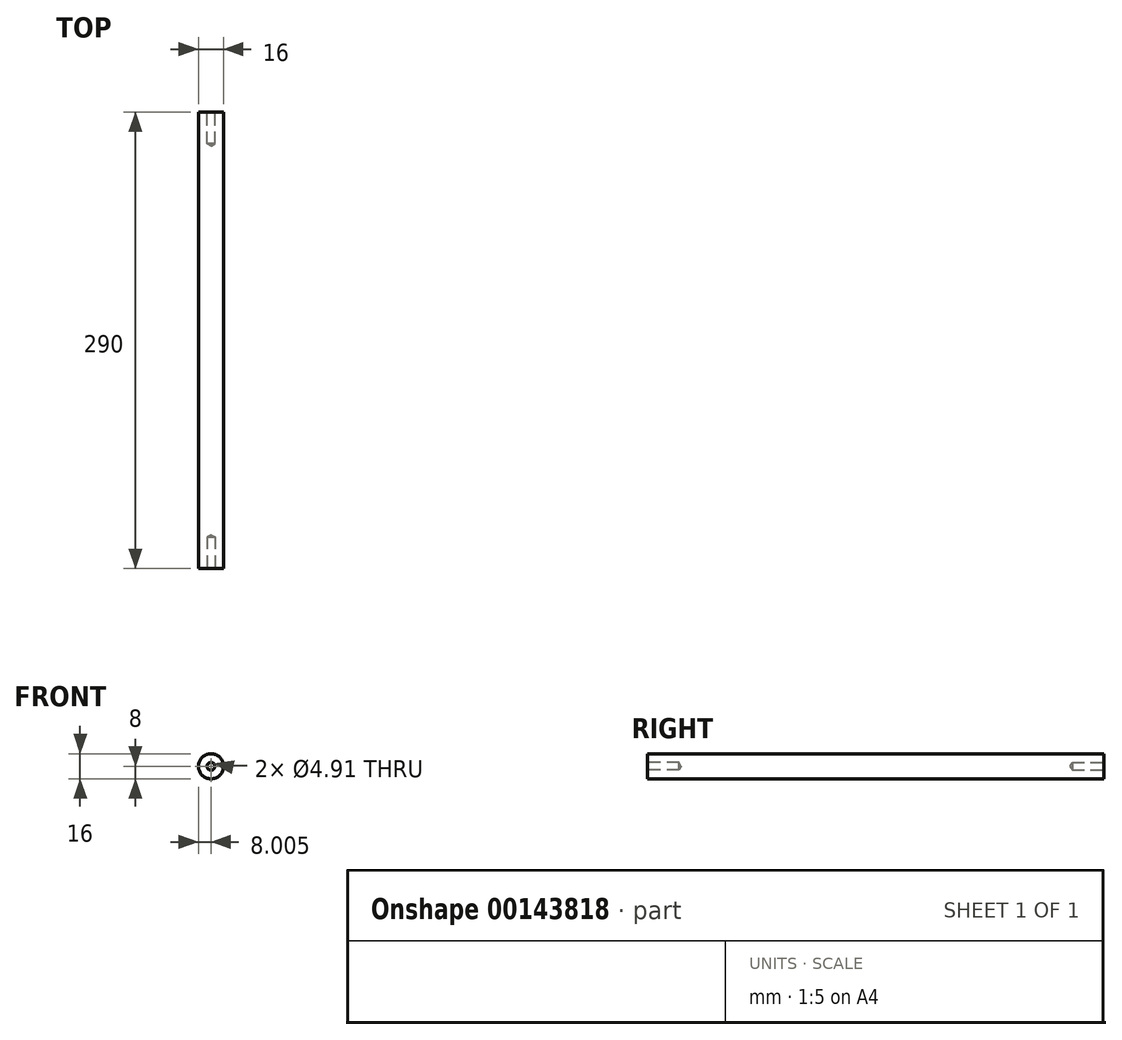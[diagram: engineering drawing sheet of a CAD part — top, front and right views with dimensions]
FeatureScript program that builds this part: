
annotation { "Feature Type Name" : "Feature", "Feature Type Description" : "" }
export const myFeature = defineFeature(function(context is Context, id is Id, definition is map)
    precondition{}
    {
        {
            var Q0;
            Q0=qCreatedBy(makeId("Front.planeOp"),FACE);
            var sketch = newSketch(context, id + "F0", { "sketchPlane" : qUnion([Q0])});
            skCircle(sketch, "E0", {"center": v(-12.95, 5.59) * mm, "radius": 8 * mm});
            skSolve(sketch);
        }
        {
            var Q0;
            Q0=makeQuery(id+"F0.imprint","IMPRINT",FACE,{"disambiguationData":[TD([[makeQuery(id+"F0.imprint","IMPRINT",EDGE,{"derivedFrom":sQuery(id+"F0.wireOp",EDGE,"E0")}),1.0]])]});
            extrude(context, id + "F1", {"entities" : qUnion([Q0]), "depth" : 290 * mm});
        }
        {
            var Q0;
            Q0=makeQuery(id+"F1.opExtrude","CAP_FACE",FACE,{"disambiguationData":[OSD([sQuery(id+"F0.wireOp",EDGE,"E0")])],"isStart":false});
            var sketch = newSketch(context, id + "F2", { "sketchPlane" : qUnion([Q0])});
            skCircle(sketch, "E1", {"center": v(-12.95, 5.59) * mm, "radius": 2.46 * mm});
            skSolve(sketch);
        }
        {
            var Q0;
            Q0=sQuery(id+"F2.wireOp",VERTEX,"E1.center");
            var Q1;
            Q1=makeQuery(id+"F1.opExtrude","SWEPT_BODY",BODY,{"disambiguationData":[OSD([sQuery(id+"F0.wireOp",EDGE,"E0")])]});
            hole(context, id + "F3", {"style" : HoleStyle.SIMPLE, "endStyle" : HoleEndStyle.BLIND, "holeDiameter" : 4.9 * mm, "holeDepth" : 20 * mm, "startFromSketch" : true, "locations" : qUnion([Q0]), "scope" : qUnion([Q1])});
        }
        {
            var Q0;
            Q0=makeQuery(id+"F1.opExtrude","CAP_FACE",FACE,{"disambiguationData":[OSD([sQuery(id+"F0.wireOp",EDGE,"E0")])],"isStart":true});
            var sketch = newSketch(context, id + "F4", { "sketchPlane" : qUnion([Q0])});
            skCircle(sketch, "E2", {"center": v(12.95, 5.59) * mm, "radius": 2.46 * mm});
            skSolve(sketch);
        }
        {
            var Q0;
            Q0=sQuery(id+"F4.wireOp",VERTEX,"E2.center");
            var Q1;
            Q1=makeQuery(id+"F1.opExtrude","SWEPT_BODY",BODY,{"disambiguationData":[OSD([sQuery(id+"F0.wireOp",EDGE,"E0")])]});
            hole(context, id + "F5", {"style" : HoleStyle.SIMPLE, "endStyle" : HoleEndStyle.BLIND, "holeDiameter" : 4.9 * mm, "holeDepth" : 20 * mm, "startFromSketch" : true, "locations" : qUnion([Q0]), "scope" : qUnion([Q1])});
        }
    });
